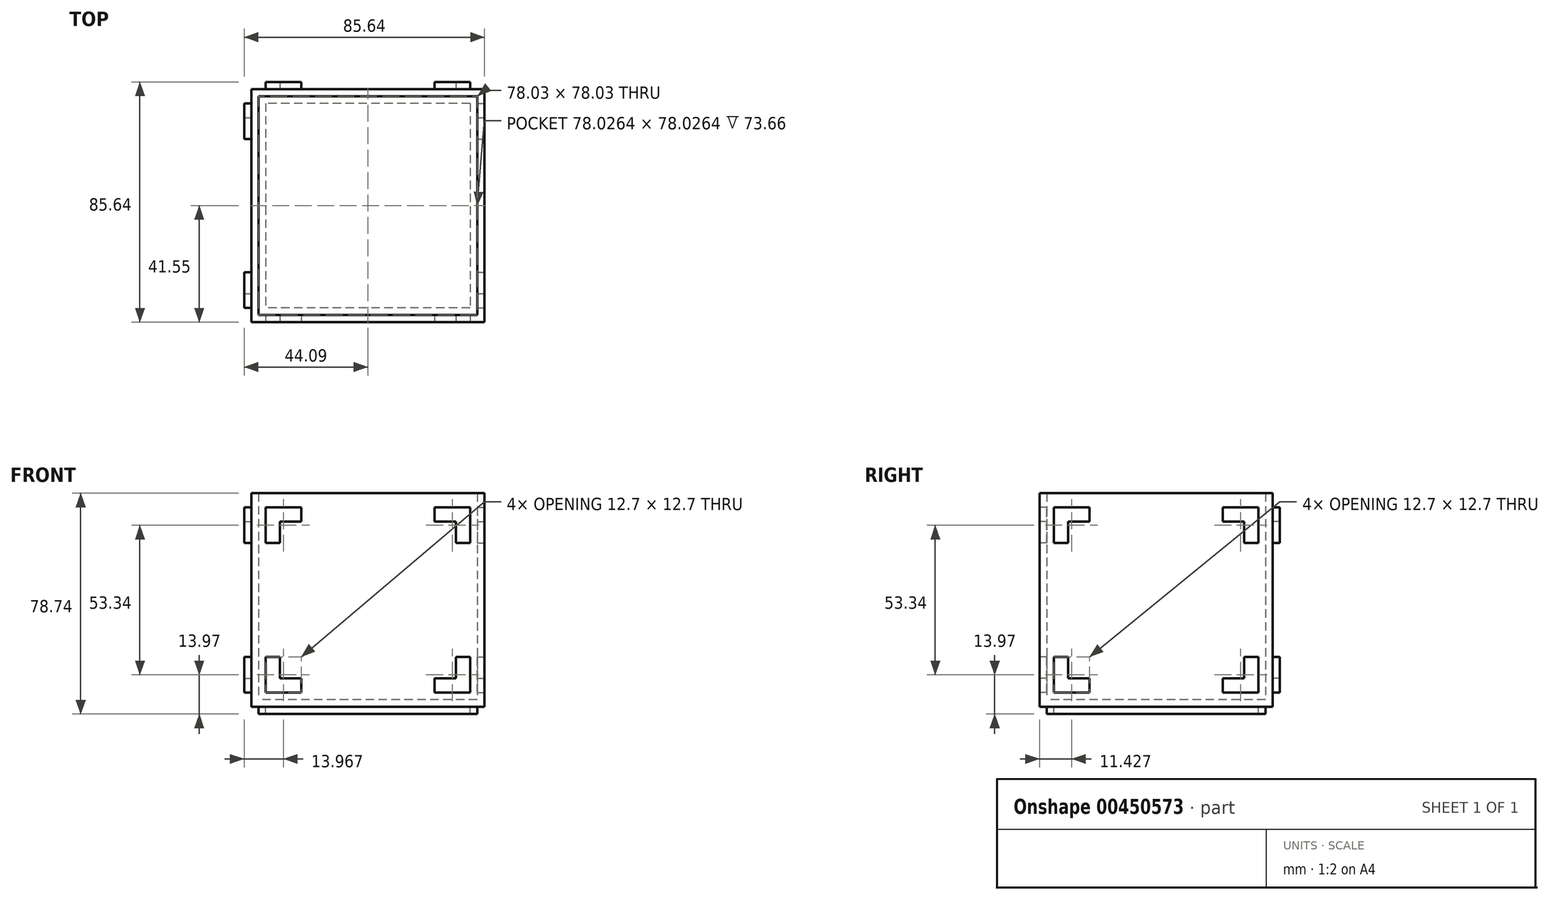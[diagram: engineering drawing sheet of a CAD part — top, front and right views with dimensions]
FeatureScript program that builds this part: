
annotation { "Feature Type Name" : "Feature", "Feature Type Description" : "" }
export const myFeature = defineFeature(function(context is Context, id is Id, definition is map)
    precondition{}
    {
        {
            var Q0;
            Q0=qCreatedBy(makeId("Top.planeOp"),FACE);
            var sketch = newSketch(context, id + "F0", { "sketchPlane" : qUnion([Q0])});
            skLineSegment(sketch, "E0.bottom", {"start": v(41.55, 41.55) * mm, "end": v(-41.55, 41.55) * mm});
            skLineSegment(sketch, "E0.top", {"start": v(41.55, -41.55) * mm, "end": v(-41.55, -41.55) * mm});
            skLineSegment(sketch, "E0.left", {"start": v(41.55, 41.55) * mm, "end": v(41.55, -41.55) * mm});
            skLineSegment(sketch, "E0.right", {"start": v(-41.55, 41.55) * mm, "end": v(-41.55, -41.55) * mm});
            skPoint(sketch, "E0.middle", {"position": v(0, 0) * mm});
            skSolve(sketch);
        }
        {
            var Q0;
            Q0=makeQuery(id+"F0.imprint","IMPRINT",FACE,{"disambiguationData":[TD([[makeQuery(id+"F0.imprint","IMPRINT",EDGE,{"derivedFrom":sQuery(id+"F0.wireOp",EDGE,"E0.bottom")}),1.0]])]});
            extrude(context, id + "F1", {"entities" : qUnion([Q0]), "depth" : 76.2 * mm});
        }
        {
            var Q0;
            Q0=makeQuery(id+"F1.opExtrude","CAP_FACE",FACE,{"disambiguationData":[OSD([sQuery(id+"F0.wireOp",EDGE,"E0.bottom"),sQuery(id+"F0.wireOp",EDGE,"E0.top"),sQuery(id+"F0.wireOp",EDGE,"E0.left"),sQuery(id+"F0.wireOp",EDGE,"E0.right")])],"isStart":false});
            shell(context, id + "F2", {"entities" : qUnion([Q0]), "thickness" : 2.54 * mm});
        }
        {
            var Q0;
            Q0=makeQuery(id+"F1.opExtrude","CAP_FACE",FACE,{"disambiguationData":[OSD([sQuery(id+"F0.wireOp",EDGE,"E0.bottom"),sQuery(id+"F0.wireOp",EDGE,"E0.top"),sQuery(id+"F0.wireOp",EDGE,"E0.left"),sQuery(id+"F0.wireOp",EDGE,"E0.right")])],"isStart":true});
            var sketch = newSketch(context, id + "F3", { "sketchPlane" : qUnion([Q0])});
            skLineSegment(sketch, "E1.0", {"start": v(-39.01, -39.01) * mm, "end": v(-39.01, 39.01) * mm});
            skLineSegment(sketch, "E1.1", {"start": v(39.01, -39.01) * mm, "end": v(-39.01, -39.01) * mm});
            skLineSegment(sketch, "E1.2", {"start": v(39.01, -39.01) * mm, "end": v(39.01, 39.01) * mm});
            skLineSegment(sketch, "E1.3", {"start": v(39.01, 39.01) * mm, "end": v(-39.01, 39.01) * mm});
            skLineSegment(sketch, "E2.0", {"start": v(36.47, -36.47) * mm, "end": v(36.47, 36.47) * mm});
            skLineSegment(sketch, "E2.1", {"start": v(36.47, -36.47) * mm, "end": v(-36.47, -36.47) * mm});
            skLineSegment(sketch, "E2.2", {"start": v(-36.47, -36.47) * mm, "end": v(-36.47, 36.47) * mm});
            skLineSegment(sketch, "E2.3", {"start": v(36.47, 36.47) * mm, "end": v(-36.47, 36.47) * mm});
            skSolve(sketch);
        }
        {
            var Q0;
            Q0=makeQuery(id+"F3.imprint","IMPRINT",FACE,{"disambiguationData":[TD([[makeQuery(id+"F3.imprint","IMPRINT",EDGE,{"derivedFrom":sQuery(id+"F3.wireOp",EDGE,"E1.0")}),-1.0]])]});
            extrude(context, id + "F4", {"entities" : qUnion([Q0]), "operationType" : NewBodyOperationType.ADD, "depth" : 2.54 * mm});
        }
        {
            var Q0;
            Q0=makeQuery(id+"F1.opExtrude","SWEPT_FACE",FACE,{"disambiguationData":[OSD([sQuery(id+"F0.wireOp",EDGE,"E0.right")])]});
            var sketch = newSketch(context, id + "F5", { "sketchPlane" : qUnion([Q0])});
            skLineSegment(sketch, "E3.0", {"start": v(-36.47, 71.12) * mm, "end": v(-36.47, 58.42) * mm});
            skLineSegment(sketch, "E3.1", {"start": v(-36.47, 71.12) * mm, "end": v(-23.77, 71.12) * mm});
            skLineSegment(sketch, "E3.2", {"start": v(36.47, 71.12) * mm, "end": v(36.47, 58.42) * mm});
            skLineSegment(sketch, "E3.3", {"start": v(-36.47, 5.08) * mm, "end": v(-23.77, 5.08) * mm});
            skLineSegment(sketch, "E4", {"start": v(-23.77, 71.12) * mm, "end": v(-23.77, 66.04) * mm});
            skLineSegment(sketch, "E5", {"start": v(-23.77, 66.04) * mm, "end": v(-31.4, 66.04) * mm});
            skLineSegment(sketch, "E6", {"start": v(-31.4, 66.04) * mm, "end": v(-31.4, 58.42) * mm});
            skLineSegment(sketch, "E7", {"start": v(-31.4, 58.42) * mm, "end": v(-36.47, 58.42) * mm});
            skLineSegment(sketch, "E8.MirrorCS", {"start": v(23.77, 71.12) * mm, "end": v(23.77, 66.04) * mm});
            skLineSegment(sketch, "E9.MirrorCS", {"start": v(31.4, 58.42) * mm, "end": v(36.47, 58.42) * mm});
            skLineSegment(sketch, "E10.MirrorCS", {"start": v(31.4, 66.04) * mm, "end": v(31.4, 58.42) * mm});
            skLineSegment(sketch, "E11.MirrorCS", {"start": v(23.77, 66.04) * mm, "end": v(31.4, 66.04) * mm});
            skLineSegment(sketch, "E12.MirrorCS", {"start": v(-31.4, 17.78) * mm, "end": v(-36.47, 17.78) * mm});
            skLineSegment(sketch, "E13.MirrorCS", {"start": v(-31.4, 10.16) * mm, "end": v(-31.4, 17.78) * mm});
            skLineSegment(sketch, "E14.MirrorCS", {"start": v(-23.77, 10.16) * mm, "end": v(-31.4, 10.16) * mm});
            skLineSegment(sketch, "E15.MirrorCS", {"start": v(-23.77, 5.08) * mm, "end": v(-23.77, 10.16) * mm});
            skLineSegment(sketch, "E16.MirrorCS", {"start": v(31.4, 17.78) * mm, "end": v(36.47, 17.78) * mm});
            skLineSegment(sketch, "E17.MirrorCS", {"start": v(31.4, 10.16) * mm, "end": v(31.4, 17.78) * mm});
            skLineSegment(sketch, "E18.MirrorCS", {"start": v(23.77, 10.16) * mm, "end": v(31.4, 10.16) * mm});
            skLineSegment(sketch, "E19.MirrorCS", {"start": v(23.77, 5.08) * mm, "end": v(23.77, 10.16) * mm});
            skLineSegment(sketch, "E20.trimOffspring", {"start": v(-36.47, 17.78) * mm, "end": v(-36.47, 5.08) * mm});
            skLineSegment(sketch, "E21.trimOffspring", {"start": v(23.77, 71.12) * mm, "end": v(36.47, 71.12) * mm});
            skLineSegment(sketch, "E22.trimOffspring", {"start": v(36.47, 17.78) * mm, "end": v(36.47, 5.08) * mm});
            skLineSegment(sketch, "E23.trimOffspring", {"start": v(23.77, 5.08) * mm, "end": v(36.47, 5.08) * mm});
            skSolve(sketch);
        }
        {
            var Q0;
            Q0=makeQuery(id+"F1.opExtrude","SWEPT_FACE",FACE,{"disambiguationData":[OSD([sQuery(id+"F0.wireOp",EDGE,"E0.top")])]});
            var sketch = newSketch(context, id + "F6", { "sketchPlane" : qUnion([Q0])});
            skLineSegment(sketch, "E24.0", {"start": v(-36.47, 5.08) * mm, "end": v(-23.77, 5.08) * mm});
            skLineSegment(sketch, "E24.1", {"start": v(-36.47, 71.12) * mm, "end": v(-36.47, 58.42) * mm});
            skLineSegment(sketch, "E24.2", {"start": v(36.47, 71.12) * mm, "end": v(23.77, 71.12) * mm});
            skLineSegment(sketch, "E24.3", {"start": v(36.47, 5.08) * mm, "end": v(36.47, 17.78) * mm});
            skLineSegment(sketch, "E25", {"start": v(-36.47, 71.12) * mm, "end": v(-23.77, 71.12) * mm});
            skLineSegment(sketch, "E26", {"start": v(-23.77, 71.12) * mm, "end": v(-23.77, 66.04) * mm});
            skLineSegment(sketch, "E27", {"start": v(-23.77, 66.04) * mm, "end": v(-31.4, 66.04) * mm});
            skLineSegment(sketch, "E28", {"start": v(-31.4, 66.04) * mm, "end": v(-31.4, 58.42) * mm});
            skLineSegment(sketch, "E29", {"start": v(-31.4, 58.42) * mm, "end": v(-36.47, 58.42) * mm});
            skLineSegment(sketch, "E30.MirrorCS", {"start": v(23.77, 66.04) * mm, "end": v(31.4, 66.04) * mm});
            skLineSegment(sketch, "E31.MirrorCS", {"start": v(31.4, 66.04) * mm, "end": v(31.4, 58.42) * mm});
            skLineSegment(sketch, "E32.MirrorCS", {"start": v(23.77, 71.12) * mm, "end": v(23.77, 66.04) * mm});
            skLineSegment(sketch, "E33.MirrorCS", {"start": v(31.4, 58.42) * mm, "end": v(36.47, 58.42) * mm});
            skLineSegment(sketch, "E34.MirrorCS", {"start": v(-31.4, 17.78) * mm, "end": v(-36.47, 17.78) * mm});
            skLineSegment(sketch, "E35.MirrorCS", {"start": v(-23.77, 5.08) * mm, "end": v(-23.77, 10.16) * mm});
            skLineSegment(sketch, "E36.MirrorCS", {"start": v(-23.77, 10.16) * mm, "end": v(-31.4, 10.16) * mm});
            skLineSegment(sketch, "E37.MirrorCS", {"start": v(-31.4, 10.16) * mm, "end": v(-31.4, 17.78) * mm});
            skLineSegment(sketch, "E38.MirrorCS", {"start": v(31.4, 17.78) * mm, "end": v(36.47, 17.78) * mm});
            skLineSegment(sketch, "E39.MirrorCS", {"start": v(31.4, 10.16) * mm, "end": v(31.4, 17.78) * mm});
            skLineSegment(sketch, "E40.MirrorCS", {"start": v(23.77, 5.08) * mm, "end": v(23.77, 10.16) * mm});
            skLineSegment(sketch, "E41.MirrorCS", {"start": v(23.77, 10.16) * mm, "end": v(31.4, 10.16) * mm});
            skPoint(sketch, "E42.orphan", {"position": v(0, 71.12) * mm});
            skPoint(sketch, "E43.end.orphan", {"position": v(36.47, 38.1) * mm});
            skPoint(sketch, "E44.end.orphan", {"position": v(-36.47, 38.1) * mm});
            skPoint(sketch, "E45.end.orphan", {"position": v(0, 5.08) * mm});
            skPoint(sketch, "E45.start.orphan", {"position": v(0, 38.1) * mm});
            skLineSegment(sketch, "E46.trimOffspring", {"start": v(-36.47, 17.78) * mm, "end": v(-36.47, 5.08) * mm});
            skLineSegment(sketch, "E47.trimOffspring", {"start": v(23.77, 5.08) * mm, "end": v(36.47, 5.08) * mm});
            skLineSegment(sketch, "E48.trimOffspring", {"start": v(36.47, 58.42) * mm, "end": v(36.47, 71.12) * mm});
            skLineSegment(sketch, "E49.trimOffspring", {"start": v(-23.77, 71.12) * mm, "end": v(-36.47, 71.12) * mm});
            skSolve(sketch);
        }
        {
            var Q0;
            Q0=makeQuery(id+"F1.opExtrude","SWEPT_FACE",FACE,{"disambiguationData":[OSD([sQuery(id+"F0.wireOp",EDGE,"E0.left")])]});
            var sketch = newSketch(context, id + "F7", { "sketchPlane" : qUnion([Q0])});
            skLineSegment(sketch, "E50.0", {"start": v(-36.47, 5.08) * mm, "end": v(-23.77, 5.08) * mm});
            skLineSegment(sketch, "E50.1", {"start": v(-36.47, 71.12) * mm, "end": v(-36.47, 58.42) * mm});
            skLineSegment(sketch, "E50.2", {"start": v(36.47, 71.12) * mm, "end": v(23.77, 71.12) * mm});
            skLineSegment(sketch, "E50.3", {"start": v(36.47, 5.08) * mm, "end": v(36.47, 17.78) * mm});
            skLineSegment(sketch, "E51", {"start": v(-36.47, 71.12) * mm, "end": v(-23.77, 71.12) * mm});
            skLineSegment(sketch, "E52", {"start": v(-23.77, 71.12) * mm, "end": v(-23.77, 66.04) * mm});
            skLineSegment(sketch, "E53", {"start": v(-23.77, 66.04) * mm, "end": v(-31.4, 66.04) * mm});
            skLineSegment(sketch, "E54", {"start": v(-31.4, 66.04) * mm, "end": v(-31.4, 58.42) * mm});
            skLineSegment(sketch, "E55", {"start": v(-31.4, 58.42) * mm, "end": v(-36.47, 58.42) * mm});
            skLineSegment(sketch, "E56.MirrorCS", {"start": v(23.77, 71.12) * mm, "end": v(23.77, 66.04) * mm});
            skLineSegment(sketch, "E57.MirrorCS", {"start": v(23.77, 66.04) * mm, "end": v(31.4, 66.04) * mm});
            skLineSegment(sketch, "E58.MirrorCS", {"start": v(31.4, 58.42) * mm, "end": v(36.47, 58.42) * mm});
            skLineSegment(sketch, "E59.MirrorCS", {"start": v(31.4, 66.04) * mm, "end": v(31.4, 58.42) * mm});
            skLineSegment(sketch, "E60.MirrorCS", {"start": v(-31.4, 17.78) * mm, "end": v(-36.47, 17.78) * mm});
            skLineSegment(sketch, "E61.MirrorCS", {"start": v(-31.4, 10.16) * mm, "end": v(-31.4, 17.78) * mm});
            skLineSegment(sketch, "E62.MirrorCS", {"start": v(-23.77, 5.08) * mm, "end": v(-23.77, 10.16) * mm});
            skLineSegment(sketch, "E63.MirrorCS", {"start": v(-23.77, 10.16) * mm, "end": v(-31.4, 10.16) * mm});
            skLineSegment(sketch, "E64.MirrorCS", {"start": v(23.77, 10.16) * mm, "end": v(31.4, 10.16) * mm});
            skLineSegment(sketch, "E65.MirrorCS", {"start": v(31.4, 17.78) * mm, "end": v(36.47, 17.78) * mm});
            skLineSegment(sketch, "E66.MirrorCS", {"start": v(23.77, 5.08) * mm, "end": v(23.77, 10.16) * mm});
            skLineSegment(sketch, "E67.MirrorCS", {"start": v(31.4, 10.16) * mm, "end": v(31.4, 17.78) * mm});
            skLineSegment(sketch, "E68.trimOffspring", {"start": v(-23.77, 71.12) * mm, "end": v(-36.47, 71.12) * mm});
            skPoint(sketch, "E69.orphan", {"position": v(0, 71.12) * mm});
            skPoint(sketch, "E70.end.orphan", {"position": v(-36.47, 38.1) * mm});
            skPoint(sketch, "E71.end.orphan", {"position": v(36.47, 38.1) * mm});
            skPoint(sketch, "E72.end.orphan", {"position": v(0, 5.08) * mm});
            skPoint(sketch, "E72.start.orphan", {"position": v(0, 38.1) * mm});
            skLineSegment(sketch, "E73.trimOffspring", {"start": v(-36.47, 17.78) * mm, "end": v(-36.47, 5.08) * mm});
            skLineSegment(sketch, "E74.trimOffspring", {"start": v(36.47, 58.42) * mm, "end": v(36.47, 71.12) * mm});
            skLineSegment(sketch, "E75.trimOffspring", {"start": v(23.77, 5.08) * mm, "end": v(36.47, 5.08) * mm});
            skSolve(sketch);
        }
        {
            var Q0;
            Q0=makeQuery(id+"F5.imprint","IMPRINT",FACE,{"disambiguationData":[TD([[makeQuery(id+"F5.imprint","IMPRINT",EDGE,{"derivedFrom":sQuery(id+"F5.wireOp",EDGE,"E3.0")}),1.0]])]});
            var Q1;
            Q1=makeQuery(id+"F5.imprint","IMPRINT",FACE,{"disambiguationData":[TD([[makeQuery(id+"F5.imprint","IMPRINT",EDGE,{"derivedFrom":sQuery(id+"F5.wireOp",EDGE,"E3.2")}),-1.0]])]});
            var Q2;
            Q2=makeQuery(id+"F5.imprint","IMPRINT",FACE,{"disambiguationData":[TD([[makeQuery(id+"F5.imprint","IMPRINT",EDGE,{"derivedFrom":sQuery(id+"F5.wireOp",EDGE,"E16.MirrorCS")}),-1.0]])]});
            var Q3;
            Q3=makeQuery(id+"F5.imprint","IMPRINT",FACE,{"disambiguationData":[TD([[makeQuery(id+"F5.imprint","IMPRINT",EDGE,{"derivedFrom":sQuery(id+"F5.wireOp",EDGE,"E12.MirrorCS")}),1.0]])]});
            extrude(context, id + "F8", {"entities" : qUnion([Q0, Q1, Q2, Q3]), "operationType" : NewBodyOperationType.ADD, "depth" : 2.54 * mm});
        }
        {
            var Q0;
            Q0=makeQuery(id+"F7.imprint","IMPRINT",FACE,{"disambiguationData":[TD([[makeQuery(id+"F7.imprint","IMPRINT",EDGE,{"derivedFrom":sQuery(id+"F7.wireOp",EDGE,"E50.1")}),1.0]])]});
            var Q1;
            Q1=makeQuery(id+"F7.imprint","IMPRINT",FACE,{"disambiguationData":[TD([[makeQuery(id+"F7.imprint","IMPRINT",EDGE,{"derivedFrom":sQuery(id+"F7.wireOp",EDGE,"E50.2")}),1.0]])]});
            var Q2;
            Q2=makeQuery(id+"F7.imprint","IMPRINT",FACE,{"disambiguationData":[TD([[makeQuery(id+"F7.imprint","IMPRINT",EDGE,{"derivedFrom":sQuery(id+"F7.wireOp",EDGE,"E50.3")}),1.0]])]});
            var Q3;
            Q3=makeQuery(id+"F7.imprint","IMPRINT",FACE,{"disambiguationData":[TD([[makeQuery(id+"F7.imprint","IMPRINT",EDGE,{"derivedFrom":sQuery(id+"F7.wireOp",EDGE,"E50.0")}),1.0]])]});
            extrude(context, id + "F9", {"entities" : qUnion([Q0, Q1, Q2, Q3]), "operationType" : NewBodyOperationType.REMOVE, "oppositeDirection" : true, "depth" : 25.4 * mm});
        }
        {
            var Q0;
            Q0=makeQuery(id+"F1.opExtrude","SWEPT_FACE",FACE,{"disambiguationData":[OSD([sQuery(id+"F0.wireOp",EDGE,"E0.bottom")])]});
            var sketch = newSketch(context, id + "F10", { "sketchPlane" : qUnion([Q0])});
            skLineSegment(sketch, "E76.0", {"start": v(-36.47, 5.08) * mm, "end": v(-23.77, 5.08) * mm});
            skLineSegment(sketch, "E76.1", {"start": v(-36.47, 71.12) * mm, "end": v(-36.47, 58.42) * mm});
            skLineSegment(sketch, "E76.2", {"start": v(36.47, 71.12) * mm, "end": v(23.77, 71.12) * mm});
            skLineSegment(sketch, "E76.3", {"start": v(36.47, 5.08) * mm, "end": v(36.47, 17.78) * mm});
            skLineSegment(sketch, "E77", {"start": v(-36.47, 71.12) * mm, "end": v(-23.77, 71.12) * mm});
            skLineSegment(sketch, "E78", {"start": v(-23.77, 71.12) * mm, "end": v(-23.77, 66.04) * mm});
            skLineSegment(sketch, "E79", {"start": v(-23.77, 66.04) * mm, "end": v(-31.4, 66.04) * mm});
            skLineSegment(sketch, "E80", {"start": v(-31.4, 66.04) * mm, "end": v(-31.4, 58.42) * mm});
            skLineSegment(sketch, "E81", {"start": v(-31.4, 58.42) * mm, "end": v(-36.47, 58.42) * mm});
            skLineSegment(sketch, "E82.MirrorCS", {"start": v(-31.4, 17.78) * mm, "end": v(-36.47, 17.78) * mm});
            skLineSegment(sketch, "E83.MirrorCS", {"start": v(-23.77, 5.08) * mm, "end": v(-23.77, 10.16) * mm});
            skLineSegment(sketch, "E84.MirrorCS", {"start": v(-31.4, 10.16) * mm, "end": v(-31.4, 17.78) * mm});
            skLineSegment(sketch, "E85.MirrorCS", {"start": v(-23.77, 10.16) * mm, "end": v(-31.4, 10.16) * mm});
            skLineSegment(sketch, "E86.MirrorCS", {"start": v(31.4, 58.42) * mm, "end": v(36.47, 58.42) * mm});
            skLineSegment(sketch, "E87.MirrorCS", {"start": v(31.4, 66.04) * mm, "end": v(31.4, 58.42) * mm});
            skLineSegment(sketch, "E88.MirrorCS", {"start": v(23.77, 71.12) * mm, "end": v(23.77, 66.04) * mm});
            skLineSegment(sketch, "E89.MirrorCS", {"start": v(23.77, 66.04) * mm, "end": v(31.4, 66.04) * mm});
            skLineSegment(sketch, "E90.MirrorCS", {"start": v(23.77, 5.08) * mm, "end": v(23.77, 10.16) * mm});
            skLineSegment(sketch, "E91.MirrorCS", {"start": v(31.4, 17.78) * mm, "end": v(36.47, 17.78) * mm});
            skLineSegment(sketch, "E92.MirrorCS", {"start": v(31.4, 10.16) * mm, "end": v(31.4, 17.78) * mm});
            skLineSegment(sketch, "E93.MirrorCS", {"start": v(23.77, 10.16) * mm, "end": v(31.4, 10.16) * mm});
            skPoint(sketch, "E94.orphan", {"position": v(0, 71.12) * mm});
            skPoint(sketch, "E95.orphan", {"position": v(36.47, 38.1) * mm});
            skPoint(sketch, "E96.start.orphan", {"position": v(0, 5.08) * mm});
            skPoint(sketch, "E97.start.orphan", {"position": v(-36.47, 38.1) * mm});
            skLineSegment(sketch, "E98.trimOffspring", {"start": v(-36.47, 17.78) * mm, "end": v(-36.47, 5.08) * mm});
            skLineSegment(sketch, "E99.trimOffspring", {"start": v(23.77, 5.08) * mm, "end": v(36.47, 5.08) * mm});
            skLineSegment(sketch, "E100.trimOffspring", {"start": v(36.47, 58.42) * mm, "end": v(36.47, 71.12) * mm});
            skSolve(sketch);
        }
        {
            var Q0;
            Q0=makeQuery(id+"F10.imprint","IMPRINT",FACE,{"disambiguationData":[TD([[makeQuery(id+"F10.imprint","IMPRINT",EDGE,{"derivedFrom":sQuery(id+"F10.wireOp",EDGE,"E76.2")}),1.0]])]});
            var Q1;
            Q1=makeQuery(id+"F10.imprint","IMPRINT",FACE,{"disambiguationData":[TD([[makeQuery(id+"F10.imprint","IMPRINT",EDGE,{"derivedFrom":sQuery(id+"F10.wireOp",EDGE,"E76.3")}),1.0]])]});
            var Q2;
            Q2=makeQuery(id+"F10.imprint","IMPRINT",FACE,{"disambiguationData":[TD([[makeQuery(id+"F10.imprint","IMPRINT",EDGE,{"derivedFrom":sQuery(id+"F10.wireOp",EDGE,"E76.0")}),1.0]])]});
            var Q3;
            Q3=makeQuery(id+"F10.imprint","IMPRINT",FACE,{"disambiguationData":[TD([[makeQuery(id+"F10.imprint","IMPRINT",EDGE,{"derivedFrom":sQuery(id+"F10.wireOp",EDGE,"E76.1")}),1.0]])]});
            extrude(context, id + "F11", {"entities" : qUnion([Q0, Q1, Q2, Q3]), "operationType" : NewBodyOperationType.ADD, "depth" : 2.54 * mm});
        }
        {
            var Q0;
            Q0=makeQuery(id+"F6.imprint","IMPRINT",FACE,{"disambiguationData":[TD([[makeQuery(id+"F6.imprint","IMPRINT",EDGE,{"derivedFrom":sQuery(id+"F6.wireOp",EDGE,"E24.1")}),1.0]])]});
            var Q1;
            Q1=makeQuery(id+"F6.imprint","IMPRINT",FACE,{"disambiguationData":[TD([[makeQuery(id+"F6.imprint","IMPRINT",EDGE,{"derivedFrom":sQuery(id+"F6.wireOp",EDGE,"E24.0")}),1.0]])]});
            var Q2;
            Q2=makeQuery(id+"F6.imprint","IMPRINT",FACE,{"disambiguationData":[TD([[makeQuery(id+"F6.imprint","IMPRINT",EDGE,{"derivedFrom":sQuery(id+"F6.wireOp",EDGE,"E24.3")}),1.0]])]});
            var Q3;
            Q3=makeQuery(id+"F6.imprint","IMPRINT",FACE,{"disambiguationData":[TD([[makeQuery(id+"F6.imprint","IMPRINT",EDGE,{"derivedFrom":sQuery(id+"F6.wireOp",EDGE,"E24.2")}),1.0]])]});
            extrude(context, id + "F12", {"entities" : qUnion([Q0, Q1, Q2, Q3]), "operationType" : NewBodyOperationType.REMOVE, "oppositeDirection" : true, "depth" : 25.4 * mm});
        }
    });
